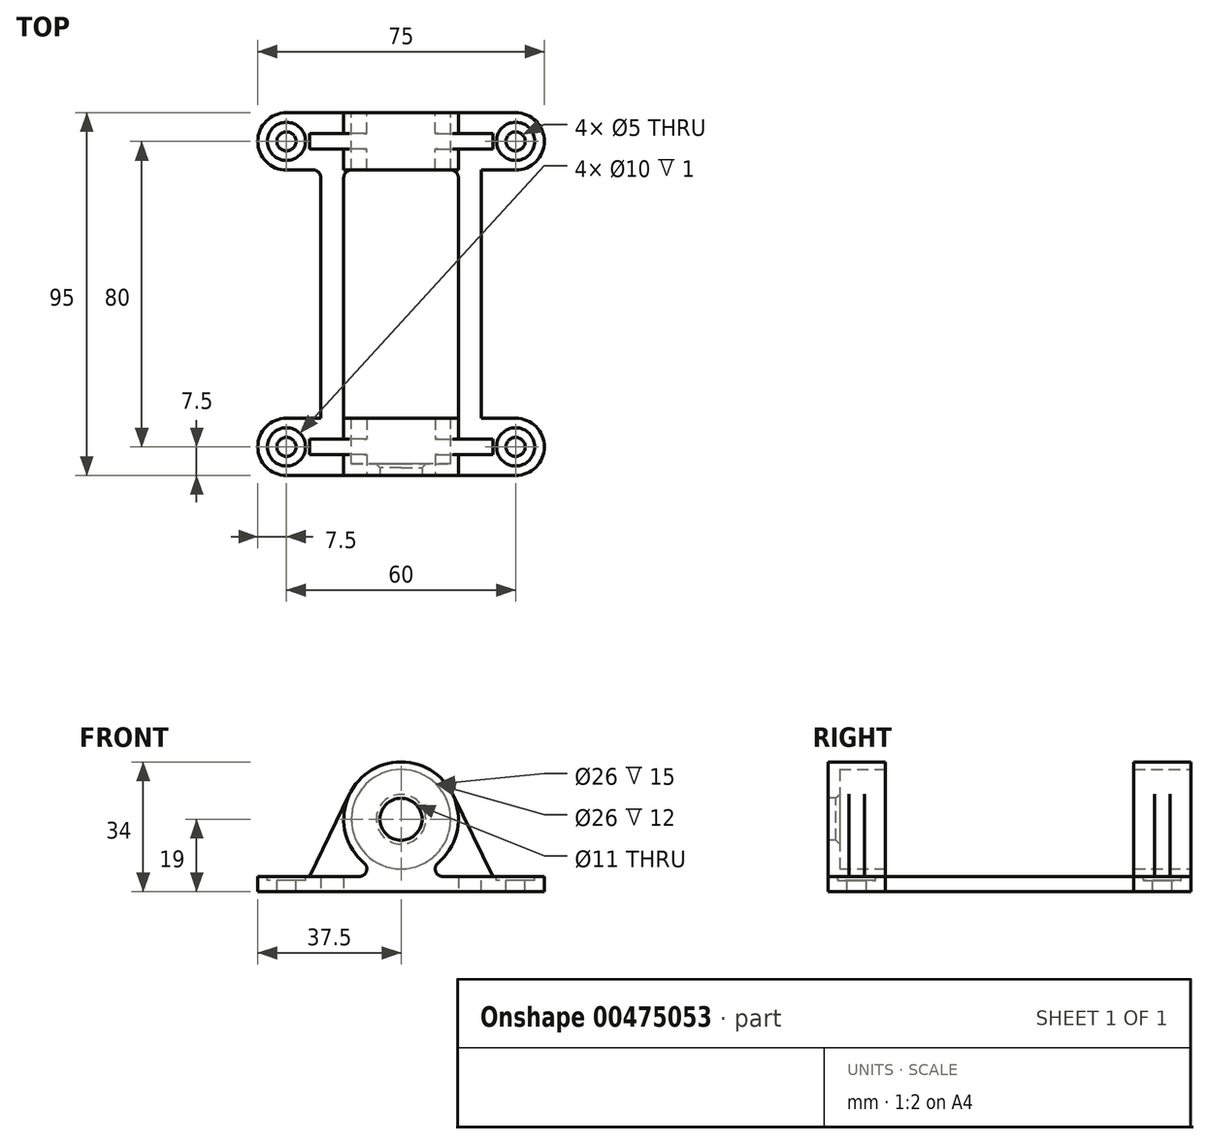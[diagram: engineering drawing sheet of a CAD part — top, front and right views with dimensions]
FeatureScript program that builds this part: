
annotation { "Feature Type Name" : "Feature", "Feature Type Description" : "" }
export const myFeature = defineFeature(function(context is Context, id is Id, definition is map)
    precondition{}
    {
        {
            assignVariable(context, id + "F0", {"name" : "Thickness", "anyValue" : 15});
        }
        {
            assignVariable(context, id + "F1", {"name" : "DistanceY", "anyValue" : 80});
        }
        {
            var Q0;
            Q0=qCreatedBy(makeId("Front.planeOp"),FACE);
            var sketch = newSketch(context, id + "F2", { "sketchPlane" : qUnion([Q0])});
            skLineSegment(sketch, "E0", {"start": v(0, 0) * mm, "end": v(-37.5, 0) * mm});
            skLineSegment(sketch, "E1", {"start": v(-37.5, 0) * mm, "end": v(-37.5, 4) * mm});
            skLineSegment(sketch, "E2", {"start": v(-37.5, 4) * mm, "end": v(-10.95, 4) * mm});
            skLineSegment(sketch, "E3", {"start": v(0, -14.72) * mm, "end": v(0, 62.74) * mm, "construction": true});
            skArc(sketch, "E4", {"start": v(-9.67, 7.53) * mm, "mid": v(-14.1, 24.14) * mm, "end": v(0, 34) * mm});
            skPoint(sketch, "E5.visualSharp", {"position": v(0, 4) * mm});
            skArc(sketch, "E5.filletArc", {"start": v(-10.95, 4) * mm, "mid": v(-9.08, 5.31) * mm, "end": v(-9.67, 7.53) * mm});
            skLineSegment(sketch, "E6.MirrorCS", {"start": v(37.5, 0) * mm, "end": v(37.5, 4) * mm});
            skLineSegment(sketch, "E7.MirrorCS", {"start": v(37.5, 4) * mm, "end": v(10.95, 4) * mm});
            skLineSegment(sketch, "E8.MirrorCS", {"start": v(0, 0) * mm, "end": v(37.5, 0) * mm});
            skArc(sketch, "E9.MirrorCS", {"start": v(9.67, 7.53) * mm, "mid": v(14.1, 24.14) * mm, "end": v(0, 34) * mm});
            skArc(sketch, "E10.MirrorCS", {"start": v(10.95, 4) * mm, "mid": v(9.08, 5.31) * mm, "end": v(9.67, 7.53) * mm});
            skArc(sketch, "E11", {"start": v(-9.67, 7.53) * mm, "mid": v(0, 4) * mm, "end": v(9.67, 7.53) * mm, "construction": true});
            skSolve(sketch);
        }
        {
            var Q0;
            Q0=qSketchRegion(id+"F2",true);
            extrude(context, id + "F3", {"entities" : qUnion([Q0]), "endBound" : BoundingType.SYMMETRIC, "depth" : 15 * mm});
        }
        {
            var Q0;
            Q0=makeQuery(id+"F3.opExtrude","CAP_EDGE",EDGE,{"disambiguationData":[OSD([sQuery(id+"F2.wireOp",EDGE,"E6.MirrorCS")])],"isStart":false});
            var Q1;
            Q1=makeQuery(id+"F3.opExtrude","CAP_EDGE",EDGE,{"disambiguationData":[OSD([sQuery(id+"F2.wireOp",EDGE,"E6.MirrorCS")])],"isStart":true});
            var Q2;
            Q2=makeQuery(id+"F3.opExtrude","CAP_EDGE",EDGE,{"disambiguationData":[OSD([sQuery(id+"F2.wireOp",EDGE,"E1")])],"isStart":false});
            var Q3;
            Q3=makeQuery(id+"F3.opExtrude","CAP_EDGE",EDGE,{"disambiguationData":[OSD([sQuery(id+"F2.wireOp",EDGE,"E1")])],"isStart":true});
            fillet(context, id + "F4", {"entities" : qUnion([Q0, Q1, Q2, Q3]), "radius" : (getVariable(context, 'Thickness') / 2) * mm, "tangentPropagation" : true, "allowEdgeOverflow" : false});
        }
        {
            var Q0;
            Q0=makeQuery(id+"F3.opExtrude","SWEPT_FACE",FACE,{"disambiguationData":[OSD([sQuery(id+"F2.wireOp",EDGE,"E7.MirrorCS")])]});
            var sketch = newSketch(context, id + "F5", { "sketchPlane" : qUnion([Q0])});
            skPoint(sketch, "E12", {"position": v(30, 0) * mm});
            skPoint(sketch, "E13.MirrorP", {"position": v(-30, 0) * mm});
            skSolve(sketch);
        }
        {
            var Q0;
            Q0=sQuery(id+"F5.wireOp",VERTEX,"E12");
            var Q1;
            Q1=sQuery(id+"F5.wireOp",VERTEX,"E13.MirrorP");
            var Q2;
            Q2=makeQuery(id+"F3.opExtrude","SWEPT_BODY",BODY,{"disambiguationData":[OSD([sQuery(id+"F2.wireOp",EDGE,"E0"),sQuery(id+"F2.wireOp",EDGE,"E1"),sQuery(id+"F2.wireOp",EDGE,"E2"),sQuery(id+"F2.wireOp",EDGE,"E5.filletArc"),sQuery(id+"F2.wireOp",EDGE,"E6.MirrorCS"),sQuery(id+"F2.wireOp",EDGE,"E7.MirrorCS"),sQuery(id+"F2.wireOp",EDGE,"E8.MirrorCS"),sQuery(id+"F2.wireOp",EDGE,"E9.MirrorCS"),sQuery(id+"F2.wireOp",EDGE,"E10.MirrorCS"),sQuery(id+"F2.wireOp",EDGE,"E4"),sQuery(id+"F2.wireOp",EDGE,"xOvTdpff-GPNy-Ahw4-pvuq-FGurvRJnDwLL"),sQuery(id+"F2.wireOp",EDGE,"c4084a71-2947-44b7-b196-35892ec3426b0.MirrorCS")])]});
            hole(context, id + "F6", {"style" : HoleStyle.C_BORE, "endStyle" : HoleEndStyle.THROUGH, "holeDiameter" : 5 * mm, "cBoreDiameter" : 10 * mm, "cBoreDepth" : 1 * mm, "isTappedThrough" : true, "tappedDepth" : 12 * mm, "tapClearance" : 3, "locations" : qUnion([Q0, Q1]), "scope" : qUnion([Q2])});
        }
        {
            var Q0;
            Q0=qCreatedBy(makeId("Front.planeOp"),FACE);
            var sketch = newSketch(context, id + "F7", { "sketchPlane" : qUnion([Q0])});
            skLineSegment(sketch, "E14", {"start": v(24, 4) * mm, "end": v(13.48, 25.57) * mm});
            skArc(sketch, "E15.0", {"start": v(9.67, 7.53) * mm, "mid": v(14.68, 15.9) * mm, "end": v(13.48, 25.57) * mm});
            skArc(sketch, "E16.0", {"start": v(10.95, 4) * mm, "mid": v(9.08, 5.31) * mm, "end": v(9.67, 7.53) * mm});
            skPoint(sketch, "E17.0", {"position": v(10.95, 4) * mm});
            skLineSegment(sketch, "E18", {"start": v(10.95, 4) * mm, "end": v(24, 4) * mm});
            skLineSegment(sketch, "E19.0", {"start": v(25, 4) * mm, "end": v(35, 4) * mm, "construction": true});
            skSolve(sketch);
        }
        {
            var Q0;
            {var subQ0=sQuery(id+"F7.wireOp",EDGE,"E14");Q0=makeQuery(id+"F7.imprint","IMPRINT",FACE,{"disambiguationData":[TD([[makeQuery(id+"F7.imprint","IMPRINT",EDGE,{"derivedFrom":subQ0}),1.0]])]});}
            extrude(context, id + "F8", {"entities" : qUnion([Q0]), "endBound" : BoundingType.SYMMETRIC, "depth" : 4 * mm});
        }
        {
            var Q0;
            Q0=makeQuery(id+"F8.opExtrude","SWEPT_BODY",BODY,{"disambiguationData":[OSD([sQuery(id+"F7.wireOp",EDGE,"E14"),sQuery(id+"F7.wireOp",EDGE,"E15.0"),sQuery(id+"F7.wireOp",EDGE,"E16.0"),sQuery(id+"F7.wireOp",EDGE,"d5b68f82-8350-41d3-9ff2-1b9ca3f2bff8.0")])]});
            var Q1;
            Q1=qCreatedBy(makeId("Right.planeOp"),FACE);
            mirror(context, id + "F9", {"operationType" : NewBodyOperationType.ADD, "entities" : qUnion([Q0]), "mirrorPlane" : qUnion([Q1])});
        }
        {
            var Q0;
            Q0=qCreatedBy(makeId("Front.planeOp"),FACE);
            cPlane(context, id + "F10", {"entities" : qUnion([Q0]), "cplaneType" : CPlaneType.OFFSET, "offset" : (getVariable(context, 'DistanceY') / 2) * mm, "width" : 150 * mm, "height" : 150 * mm});
        }
        {
            var Q0;
            Q0=makeQuery(id+"F3.opExtrude","SWEPT_BODY",BODY,{"disambiguationData":[OSD([sQuery(id+"F2.wireOp",EDGE,"E0"),sQuery(id+"F2.wireOp",EDGE,"E1"),sQuery(id+"F2.wireOp",EDGE,"E2"),sQuery(id+"F2.wireOp",EDGE,"E5.filletArc"),sQuery(id+"F2.wireOp",EDGE,"E6.MirrorCS"),sQuery(id+"F2.wireOp",EDGE,"E7.MirrorCS"),sQuery(id+"F2.wireOp",EDGE,"E8.MirrorCS"),sQuery(id+"F2.wireOp",EDGE,"E9.MirrorCS"),sQuery(id+"F2.wireOp",EDGE,"E10.MirrorCS"),sQuery(id+"F2.wireOp",EDGE,"E4")])]});
            var Q1;
            Q1=qCreatedBy(id+"F10.planeOp",FACE);
            mirror(context, id + "F11", {"entities" : qUnion([Q0]), "mirrorPlane" : qUnion([Q1])});
        }
        {
            var Q0;
            Q0=makeQuery(id+"F3.opExtrude","CAP_FACE",FACE,{"disambiguationData":[OSD([sQuery(id+"F2.wireOp",EDGE,"E0"),sQuery(id+"F2.wireOp",EDGE,"E1"),sQuery(id+"F2.wireOp",EDGE,"E2"),sQuery(id+"F2.wireOp",EDGE,"E5.filletArc"),sQuery(id+"F2.wireOp",EDGE,"E6.MirrorCS"),sQuery(id+"F2.wireOp",EDGE,"E7.MirrorCS"),sQuery(id+"F2.wireOp",EDGE,"E8.MirrorCS"),sQuery(id+"F2.wireOp",EDGE,"E9.MirrorCS"),sQuery(id+"F2.wireOp",EDGE,"E10.MirrorCS"),sQuery(id+"F2.wireOp",EDGE,"E4")])],"isStart":true});
            var sketch = newSketch(context, id + "F12", { "sketchPlane" : qUnion([Q0])});
            skCircle(sketch, "E20", {"center": v(0, 19) * mm, "radius": 13 * mm});
            skSolve(sketch);
        }
        {
            var Q0;
            Q0 = qSketchRegion(id + "F12", true);
            extrude(context, id + "F13", {"entities" : qUnion([Q0]), "operationType" : NewBodyOperationType.REMOVE, "oppositeDirection" : true, "depth" : (getVariable(context, 'DistanceY') + getVariable(context, 'Thickness') - 3) * mm});
        }
        {
            var Q0;
            Q0=makeQuery(id+"F11.opPattern","COPY",FACE,{"derivedFrom":makeQuery(id+"F3.opExtrude","CAP_FACE",FACE,{"disambiguationData":[OSD([sQuery(id+"F2.wireOp",EDGE,"E0"),sQuery(id+"F2.wireOp",EDGE,"E1"),sQuery(id+"F2.wireOp",EDGE,"E2"),sQuery(id+"F2.wireOp",EDGE,"E5.filletArc"),sQuery(id+"F2.wireOp",EDGE,"E6.MirrorCS"),sQuery(id+"F2.wireOp",EDGE,"E7.MirrorCS"),sQuery(id+"F2.wireOp",EDGE,"E8.MirrorCS"),sQuery(id+"F2.wireOp",EDGE,"E9.MirrorCS"),sQuery(id+"F2.wireOp",EDGE,"E10.MirrorCS"),sQuery(id+"F2.wireOp",EDGE,"E4")])],"isStart":true}),"instanceName":"1"});
            var sketch = newSketch(context, id + "F14", { "sketchPlane" : qUnion([Q0])});
            skCircle(sketch, "E21", {"center": v(0, 19) * mm, "radius": 5.5 * mm});
            skSolve(sketch);
        }
        {
            var Q0;
            Q0 = qSketchRegion(id + "F14", true);
            extrude(context, id + "F15", {"entities" : qUnion([Q0]), "operationType" : NewBodyOperationType.REMOVE, "endBound" : BoundingType.THROUGH_ALL, "oppositeDirection" : true, "depth" : 25 * mm});
        }
        {
            var Q0;
            Q0=makeQuery(id+"F3.opExtrude","CAP_FACE",FACE,{"disambiguationData":[OSD([sQuery(id+"F2.wireOp",EDGE,"E0"),sQuery(id+"F2.wireOp",EDGE,"E1"),sQuery(id+"F2.wireOp",EDGE,"E2"),sQuery(id+"F2.wireOp",EDGE,"E5.filletArc"),sQuery(id+"F2.wireOp",EDGE,"E6.MirrorCS"),sQuery(id+"F2.wireOp",EDGE,"E7.MirrorCS"),sQuery(id+"F2.wireOp",EDGE,"E8.MirrorCS"),sQuery(id+"F2.wireOp",EDGE,"E9.MirrorCS"),sQuery(id+"F2.wireOp",EDGE,"E10.MirrorCS"),sQuery(id+"F2.wireOp",EDGE,"E4")])],"isStart":false});
            var sketch = newSketch(context, id + "F16", { "sketchPlane" : qUnion([Q0])});
            skLineSegment(sketch, "E22.bottom", {"start": v(15, 0) * mm, "end": v(21, 0) * mm});
            skLineSegment(sketch, "E22.top", {"start": v(15, 4) * mm, "end": v(21, 4) * mm});
            skLineSegment(sketch, "E22.left", {"start": v(15, 0) * mm, "end": v(15, 4) * mm});
            skLineSegment(sketch, "E22.right", {"start": v(21, 0) * mm, "end": v(21, 4) * mm});
            skLineSegment(sketch, "E23.MirrorCS", {"start": v(-15, 0) * mm, "end": v(-15, 4) * mm});
            skLineSegment(sketch, "E24.MirrorCS", {"start": v(-21, 0) * mm, "end": v(-21, 4) * mm});
            skLineSegment(sketch, "E25.MirrorCS", {"start": v(-15, 4) * mm, "end": v(-21, 4) * mm});
            skLineSegment(sketch, "E26.MirrorCS", {"start": v(-15, 0) * mm, "end": v(-21, 0) * mm});
            skSolve(sketch);
        }
        {
            var Q0;
            Q0 = qSketchRegion(id + "F16", true);
            extrude(context, id + "F17", {"entities" : qUnion([Q0]), "operationType" : NewBodyOperationType.ADD, "endBound" : BoundingType.UP_TO_NEXT, "depth" : 25 * mm});
        }
        {
            var Q0;
            Q0=makeQuery(id+"F17.opExtrude","CAP_EDGE",EDGE,{"disambiguationData":[OSD([sQuery(id+"F16.wireOp",EDGE,"E22.right")])],"isStart":true});
            var Q1;
            Q1=makeQuery(id+"F17.opExtrude","CAP_EDGE",EDGE,{"disambiguationData":[OSD([sQuery(id+"F16.wireOp",EDGE,"E22.left")])],"isStart":true});
            var Q2;
            Q2=makeQuery(id+"F17.opExtrude","TWEAK_EDGE",EDGE,{"derivedFrom":[makeQuery(id+"F11.opPattern","COPY",FACE,{"derivedFrom":makeQuery(id+"F3.opExtrude","CAP_FACE",FACE,{"disambiguationData":[OSD([sQuery(id+"F2.wireOp",EDGE,"E0"),sQuery(id+"F2.wireOp",EDGE,"E1"),sQuery(id+"F2.wireOp",EDGE,"E2"),sQuery(id+"F2.wireOp",EDGE,"E5.filletArc"),sQuery(id+"F2.wireOp",EDGE,"E6.MirrorCS"),sQuery(id+"F2.wireOp",EDGE,"E7.MirrorCS"),sQuery(id+"F2.wireOp",EDGE,"E8.MirrorCS"),sQuery(id+"F2.wireOp",EDGE,"E9.MirrorCS"),sQuery(id+"F2.wireOp",EDGE,"E10.MirrorCS"),sQuery(id+"F2.wireOp",EDGE,"E4")])],"isStart":false}),"instanceName":"1"}),makeQuery(id+"F16.imprint","IMPRINT",EDGE,{"derivedFrom":sQuery(id+"F16.wireOp",EDGE,"E22.right")})]});
            var Q3;
            Q3=makeQuery(id+"F17.opExtrude","TWEAK_EDGE",EDGE,{"derivedFrom":[makeQuery(id+"F11.opPattern","COPY",FACE,{"derivedFrom":makeQuery(id+"F3.opExtrude","CAP_FACE",FACE,{"disambiguationData":[OSD([sQuery(id+"F2.wireOp",EDGE,"E0"),sQuery(id+"F2.wireOp",EDGE,"E1"),sQuery(id+"F2.wireOp",EDGE,"E2"),sQuery(id+"F2.wireOp",EDGE,"E5.filletArc"),sQuery(id+"F2.wireOp",EDGE,"E6.MirrorCS"),sQuery(id+"F2.wireOp",EDGE,"E7.MirrorCS"),sQuery(id+"F2.wireOp",EDGE,"E8.MirrorCS"),sQuery(id+"F2.wireOp",EDGE,"E9.MirrorCS"),sQuery(id+"F2.wireOp",EDGE,"E10.MirrorCS"),sQuery(id+"F2.wireOp",EDGE,"E4")])],"isStart":false}),"instanceName":"1"}),makeQuery(id+"F16.imprint","IMPRINT",EDGE,{"derivedFrom":sQuery(id+"F16.wireOp",EDGE,"E22.left")})]});
            var Q4;
            Q4=makeQuery(id+"F17.opExtrude","CAP_EDGE",EDGE,{"disambiguationData":[OSD([sQuery(id+"F16.wireOp",EDGE,"E24.MirrorCS")])],"isStart":true});
            var Q5;
            Q5=makeQuery(id+"F17.opExtrude","TWEAK_EDGE",EDGE,{"derivedFrom":[makeQuery(id+"F11.opPattern","COPY",FACE,{"derivedFrom":makeQuery(id+"F3.opExtrude","CAP_FACE",FACE,{"disambiguationData":[OSD([sQuery(id+"F2.wireOp",EDGE,"E0"),sQuery(id+"F2.wireOp",EDGE,"E1"),sQuery(id+"F2.wireOp",EDGE,"E2"),sQuery(id+"F2.wireOp",EDGE,"E5.filletArc"),sQuery(id+"F2.wireOp",EDGE,"E6.MirrorCS"),sQuery(id+"F2.wireOp",EDGE,"E7.MirrorCS"),sQuery(id+"F2.wireOp",EDGE,"E8.MirrorCS"),sQuery(id+"F2.wireOp",EDGE,"E9.MirrorCS"),sQuery(id+"F2.wireOp",EDGE,"E10.MirrorCS"),sQuery(id+"F2.wireOp",EDGE,"E4")])],"isStart":false}),"instanceName":"1"}),makeQuery(id+"F16.imprint","IMPRINT",EDGE,{"derivedFrom":sQuery(id+"F16.wireOp",EDGE,"E24.MirrorCS")})]});
            var Q6;
            Q6=makeQuery(id+"F17.opExtrude","TWEAK_EDGE",EDGE,{"derivedFrom":[makeQuery(id+"F11.opPattern","COPY",FACE,{"derivedFrom":makeQuery(id+"F3.opExtrude","CAP_FACE",FACE,{"disambiguationData":[OSD([sQuery(id+"F2.wireOp",EDGE,"E0"),sQuery(id+"F2.wireOp",EDGE,"E1"),sQuery(id+"F2.wireOp",EDGE,"E2"),sQuery(id+"F2.wireOp",EDGE,"E5.filletArc"),sQuery(id+"F2.wireOp",EDGE,"E6.MirrorCS"),sQuery(id+"F2.wireOp",EDGE,"E7.MirrorCS"),sQuery(id+"F2.wireOp",EDGE,"E8.MirrorCS"),sQuery(id+"F2.wireOp",EDGE,"E9.MirrorCS"),sQuery(id+"F2.wireOp",EDGE,"E10.MirrorCS"),sQuery(id+"F2.wireOp",EDGE,"E4")])],"isStart":false}),"instanceName":"1"}),makeQuery(id+"F16.imprint","IMPRINT",EDGE,{"derivedFrom":sQuery(id+"F16.wireOp",EDGE,"E23.MirrorCS")})]});
            var Q7;
            Q7=makeQuery(id+"F17.opExtrude","CAP_EDGE",EDGE,{"disambiguationData":[OSD([sQuery(id+"F16.wireOp",EDGE,"E23.MirrorCS")])],"isStart":true});
            fillet(context, id + "F18", {"entities" : qUnion([Q0, Q1, Q2, Q3, Q4, Q5, Q6, Q7]), "radius" : 2 * mm, "tangentPropagation" : true, "allowEdgeOverflow" : false});
        }
        {
            var Q0;
            Q0=makeQuery(id+"F15.boolean.opBoolean","INTERSECT",EDGE,{"derivedFrom":[makeQuery(id+"F13.boolean.opBoolean","COPY",FACE,{"derivedFrom":makeQuery(id+"F13.opExtrude","CAP_FACE",FACE,{"disambiguationData":[OSD([sQuery(id+"F12.wireOp",EDGE,"E20")])],"isStart":false})}),makeQuery(id+"F15.opExtrude","SWEPT_FACE",FACE,{"disambiguationData":[OSD([sQuery(id+"F14.wireOp",EDGE,"E21")])]})]});
            chamfer(context, id + "F19", {"entities" : qUnion([Q0]), "width" : 1 * mm, "tangentPropagation" : true});
        }
    });
